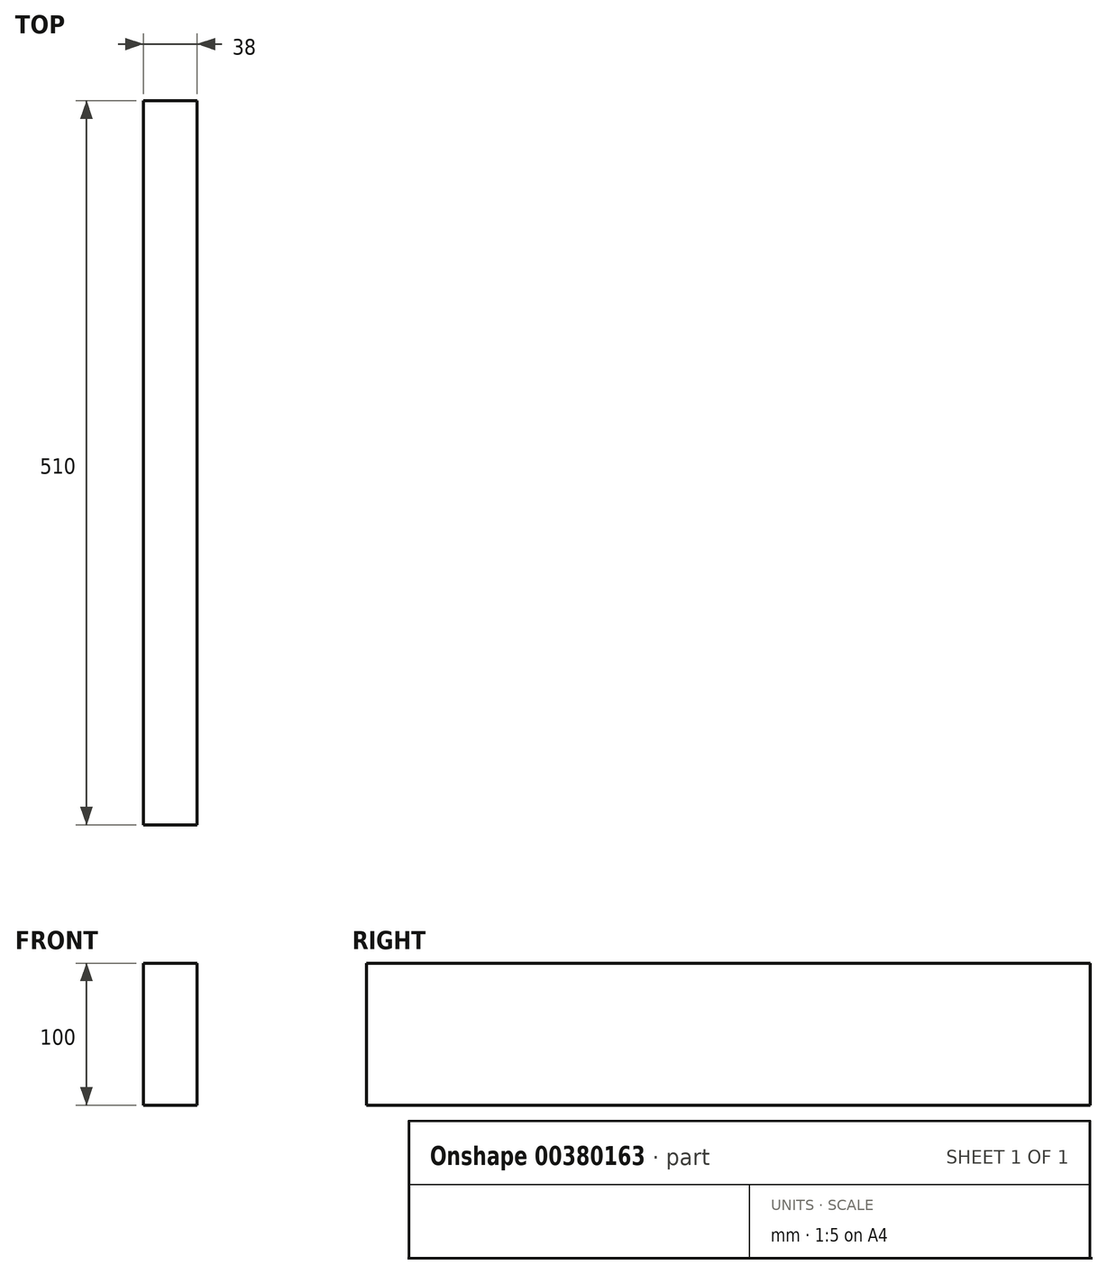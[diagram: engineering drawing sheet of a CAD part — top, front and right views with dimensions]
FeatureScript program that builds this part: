
annotation { "Feature Type Name" : "Feature", "Feature Type Description" : "" }
export const myFeature = defineFeature(function(context is Context, id is Id, definition is map)
    precondition{}
    {
        {
            var Q0;
            Q0=qCreatedBy(makeId("Front.planeOp"),FACE);
            var sketch = newSketch(context, id + "F0", { "sketchPlane" : qUnion([Q0])});
            skLineSegment(sketch, "E0.bottom", {"start": v(19, -50) * mm, "end": v(-19, -50) * mm});
            skLineSegment(sketch, "E0.top", {"start": v(19, 50) * mm, "end": v(-19, 50) * mm});
            skLineSegment(sketch, "E0.left", {"start": v(19, -50) * mm, "end": v(19, 50) * mm});
            skLineSegment(sketch, "E0.right", {"start": v(-19, -50) * mm, "end": v(-19, 50) * mm});
            skPoint(sketch, "E0.middle", {"position": v(0, 0) * mm});
            skSolve(sketch);
        }
        {
            var Q0;
            Q0 = qSketchRegion(id + "F0", true);
            extrude(context, id + "F1", {"entities" : qUnion([Q0]), "depth" : 510 * mm});
        }
    });
